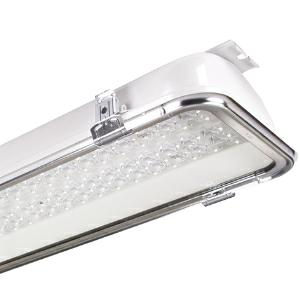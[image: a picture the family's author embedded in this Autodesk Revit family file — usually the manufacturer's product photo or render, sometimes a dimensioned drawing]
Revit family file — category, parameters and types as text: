
# Revit family: 3f_filippi_-_beta_235_76_vt_ampio_3f_filippi_-_52853_-_beta_235_led_762x45_ampio_vt_l1265
name_source: partatom
category: Lighting Fixtures
units: mm (PartAtom-declared; Revit-internal decimal feet)

## family parameters
Cut with Voids When Loaded = No
Host = Face
Light Source = No
Part Type = Normal
Room Calculation Point = No
Round Connector Dimension = Use Diameter
Shared = No

## types (1)
- 3F Filippi - Beta 235 76 VT Ampio (1 x LED, 14468 lm, 92 W, 4000 K)
    Apparent Load = 92 VA
    Approval mark = CE
    CIE Flux Codes = 55 92 99 100 100
    Color Rendering = 80
    Color Temperature = 4000 K
    Control Gear = Electronic ballast
    Default Elevation = 1800 mm
    Description = ILLUMINOTECHNICAL
Luminous efficiency 100% (DLOR 100%, ULOR 0%).
Initial luminous flux of the luminaire 14468 lm.
Wide symmetric distribution.
Installation Interdistance Transv.D = 1.18 x hu - Long.D = 1.19 x hu.
Tabular UGR (CIE 117 - 4H-8H; S=0.25H; 70/50/20): RUG 22.2 - 23.9.
Beam angle: 100° - 106°.
Luminous efficacy 157 lm/W.
Lifetime (L93/B10): 30000 h. (tq+25°C)
Lifetime (L90/B10): 50000 h. (tq+25°C)
Lifetime (L85/B10): 80000 h. (tq+25°C)
Lifetime (L80/B10): 100000 h. (tq+25°C)
Lifetime (L85/B10): 50000 h. (tq+45°C)
Sudden decreased luminous flux after 50000 hours: 0% (C0).
Photobiological safety in compliance with IEC/TR 62778: RG0 risk exempt, (IEC 62471).
In compliance with IEC/EN 62722-2-1 - IEC/EN 62717 standards.

SOURCE
2 linear LED modules 45W/840.
Energy efficiency class (UE 2019/2020 - UE 2019/2015): C.
CIE 13.3 Colour rendering index: CRI >80 (R9 <50%).
IES TM-30 Fidelity Index: Rf = 84 Rg = 95.
CCT nominal colour temperature 4000 K.
Colour initial tolerance (MacAdam): SDCM 3.

MECHANICAL
Single-piece housing in pressed steel, powder-coated in white epoxy-polyester.
VT transparent glass, non-combustible, single-piece perimeter frame in galvanised steel.
Ecologic anti-aging injected sealing gasket.
Oversized gear-tray reflector unit in highly reflective white painted hot-galvanised steel.
Methacrylate (PMMA) lenses with external flat surface.
Galvanised steel snap-lock clips for diffuser mounting (safety n° 4 per fixture).
Luminaire with limited surface temperature. - D - (EN 60598-2-24)
Dimensions: 1265x235 mm, height 105 mm. Weight 9.98 kg.
IP66 protection degree.
Mechanical strength to impacts IK09 (10 joule).
Glow-wire test resistance 960°C.

ELECTRICAL
Halogen Free electronic wiring 230V-50/60Hz, power factor 0.95, THD <25%, constant output current, class I, 1 driver.
Power of the luminaire 92 W.
ENEC - CE.
Flicker: <4%.
Luminaire compliant with EN 60598-2-22 for power supply from a centralised emergency system CPSS (Central Power Supply System), not incorporated in the luminaire - high risk areas excluded. The default power and flux are 100% in AC and 100% in DC.
Ambient temperature from -20°C to +45°C.
Temperature class T6 max 85°C.
Quick connection via M20 3P connector with 9-13 mm tightening range.
Relative humidity UR: <85%.

INSTALLATION
Ceiling / Suspended / Wall.
All accessories dedicated to this product are available on the Catalog and on our website www.3F-Filippi.com.

APPLICATIONS
Dry, dusty indoor environments, subject to occasional water splashes.
Industrial environments, warehouses, environments where security locks are required on all clips, e.g. prisons (on request).
Environments in which it is necessary a total protection against falling fragments (eg environments with foodstuffs or machines with moving parts or with extreme temperature changes), use luminaires with laminated glass.
Tempered glass is not immune to falling fragments from harmless and caused by shocks or exceptionally derived from the tempering process.

WARNING
Fixture not suitable for cold stores with an ambient temperature <0°C and/or relative humidity >85%.
Luminaire designed for disposal/recycling at end-of-life.
Replaceable (LED only) light source by a professional. Replaceable control gear by a professional.
    Height = 105 mm
    Lamp = 1 x LED
    Lamp Light Flux = 14468 lm
    Lamp Power = 92 W
    Lamp count = 1
    Length = 1265 mm
    Lifetime = 50000 h
    Luminous efficacy = 157 lm/W
    Manufacturer = 3F Filippi
    ModVariant = No
    Model = 3F Filippi - 52853 - Beta 235 LED 762x45 AMPIO VT L1265
    Mounting Place = Ceiling
    Mounting Type = Pendant
    Number of Poles = 1
    OnlyDefault = Yes
    Power Factor = 1
    Product Name = 3F Filippi - Beta 235 76 VT Ampio
    Product group = pendant luminaire
    ProductGroupID = 9
    Protection Class = Protection class I
    Protection Degree = IP 66
    RLX_Detail_Level = 1
    RLX_Emergency_Light_Flux = 0 lm
    RLX_Emergency_Type = 0
    RLX_Emergency_Type_DB = No
    RlxData = <blob elided: 88549 chars, md5=46ee711f>
    Socket = socket
    Standby Power = 0 W
    System Light Flux = 14468 lm
    System Power = 92 W
    Type Comments = Product without accessories
    Type Image = 3ffilippi_52853.jpg
    URL = http://relux.com
    VarID = ---
    Voltage = 0 V
    Weight = 0.00 kg
    Width = 235 mm

## geometry (parser evidence)
native form markers: Blend x4, Sweep x13
no freeform markers — native parametric forms only
